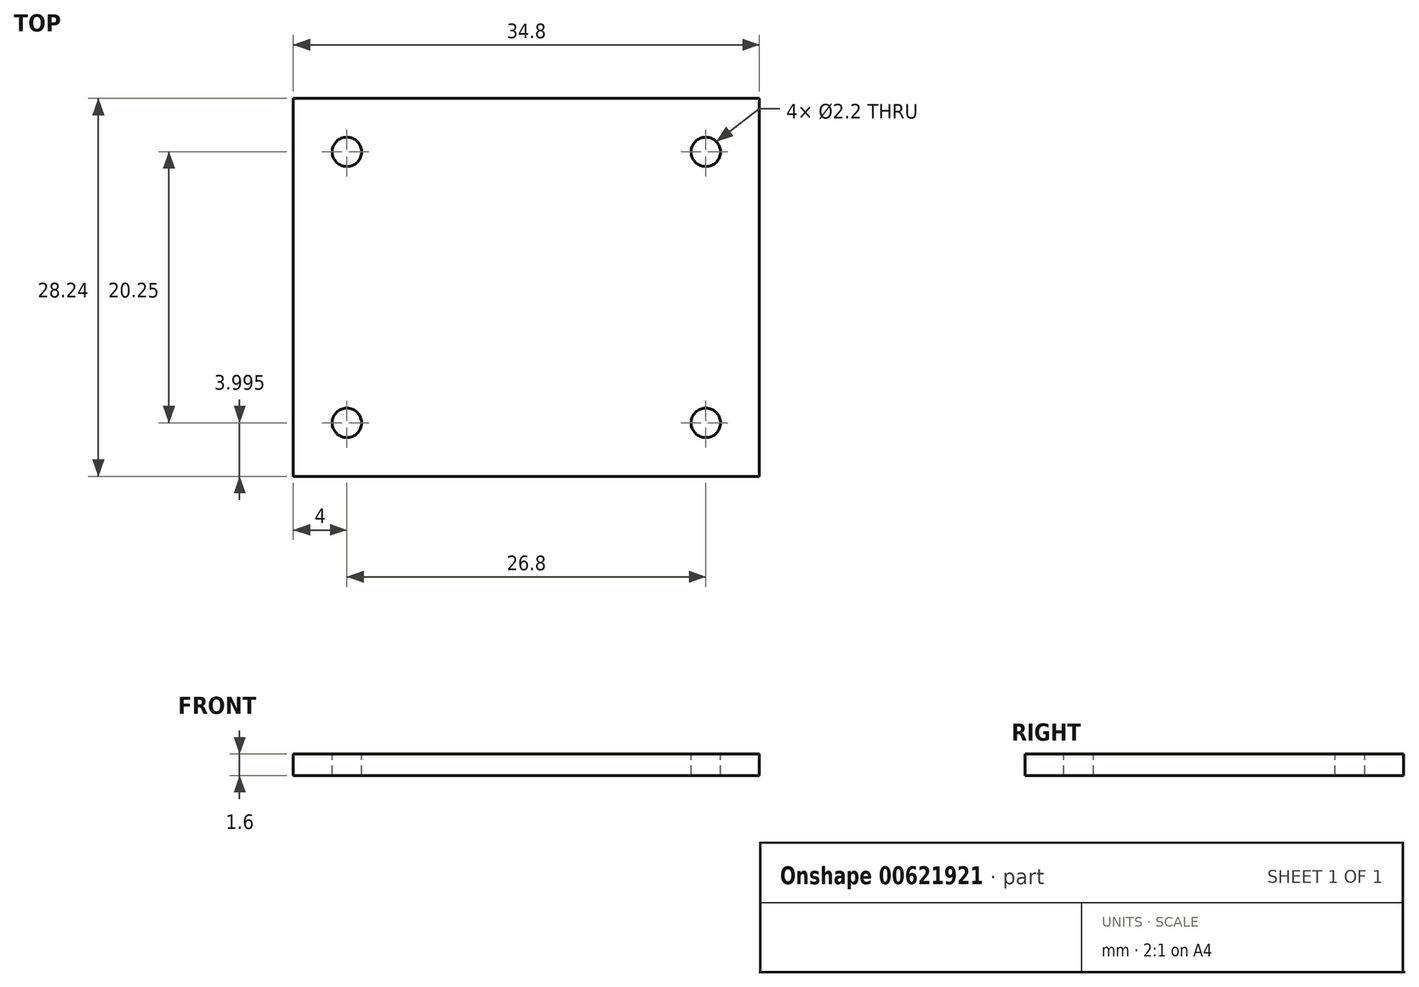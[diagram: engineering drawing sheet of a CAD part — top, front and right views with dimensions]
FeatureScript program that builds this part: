
annotation { "Feature Type Name" : "Feature", "Feature Type Description" : "" }
export const myFeature = defineFeature(function(context is Context, id is Id, definition is map)
    precondition{}
    {
        {
            var Q0;
            Q0=qCreatedBy(makeId("Top.planeOp"),FACE);
            var sketch = newSketch(context, id + "F0", { "sketchPlane" : qUnion([Q0])});
            skLineSegment(sketch, "E0.bottom", {"start": v(-17.4, 14.12) * mm, "end": v(17.4, 14.12) * mm});
            skLineSegment(sketch, "E0.top", {"start": v(-17.4, -14.13) * mm, "end": v(17.4, -14.13) * mm});
            skLineSegment(sketch, "E0.left", {"start": v(-17.4, 14.12) * mm, "end": v(-17.4, -14.13) * mm});
            skLineSegment(sketch, "E0.right", {"start": v(17.4, 14.12) * mm, "end": v(17.4, -14.12) * mm});
            skLineSegment(sketch, "E1", {"start": v(-17.4, 14.13) * mm, "end": v(17.4, -14.13) * mm});
            skSolve(sketch);
        }
        {
            var Q0;
            Q0=makeQuery(id+"F0.imprint","IMPRINT",FACE,{"disambiguationData":[TD([[makeQuery(id+"F0.imprint","IMPRINT",EDGE,{"derivedFrom":sQuery(id+"F0.wireOp",EDGE,"E0.top")}),1.0]])]});
            var Q1;
            Q1=makeQuery(id+"F0.imprint","IMPRINT",FACE,{"disambiguationData":[TD([[makeQuery(id+"F0.imprint","IMPRINT",EDGE,{"derivedFrom":sQuery(id+"F0.wireOp",EDGE,"E0.bottom")}),-1.0]])]});
            extrude(context, id + "F1", {"entities" : qUnion([Q0, Q1]), "depth" : 1.6 * mm, "offsetDistance" : 25 * mm});
        }
        {
            var Q0;
            Q0=makeQuery(id+"F1.opExtrude","CAP_FACE",FACE,{"disambiguationData":[OSD([sQuery(id+"F0.wireOp",EDGE,"E0.bottom"),sQuery(id+"F0.wireOp",EDGE,"E0.top"),sQuery(id+"F0.wireOp",EDGE,"E0.left"),sQuery(id+"F0.wireOp",EDGE,"E0.right")])],"isStart":false});
            var sketch = newSketch(context, id + "F2", { "sketchPlane" : qUnion([Q0])});
            skCircle(sketch, "E2", {"center": v(-13.4, -10.13) * mm, "radius": 1.1 * mm});
            skCircle(sketch, "E3", {"center": v(-13.4, 10.12) * mm, "radius": 1.1 * mm});
            skCircle(sketch, "E4", {"center": v(13.4, 10.12) * mm, "radius": 1.1 * mm});
            skCircle(sketch, "E5", {"center": v(13.4, -10.13) * mm, "radius": 1.1 * mm});
            skLineSegment(sketch, "E6", {"start": v(-13.4, 10.12) * mm, "end": v(-13.4, -10.13) * mm});
            skLineSegment(sketch, "E7", {"start": v(-13.4, -10.13) * mm, "end": v(13.4, -10.13) * mm});
            skLineSegment(sketch, "E8", {"start": v(13.4, -10.13) * mm, "end": v(13.4, 10.12) * mm});
            skLineSegment(sketch, "E9", {"start": v(-13.4, 10.12) * mm, "end": v(13.4, 10.12) * mm});
            skSolve(sketch);
        }
        {
            var Q0;
            {var subQ0=sQuery(id+"F2.wireOp",EDGE,"E6");var subQ1=sQuery(id+"F2.wireOp",EDGE,"E3");var subQ2=makeQuery(id+"F2.imprint","INTERSECT",VERTEX,{"derivedFrom":[subQ1,subQ0]});Q0=makeQuery(id+"F2.imprint","IMPRINT",FACE,{"disambiguationData":[TD([[makeQuery(id+"F2.imprint","IMPRINT",EDGE,{"disambiguationData":[TD([[subQ2,-1.0]])],"derivedFrom":subQ1}),1.0]])]});}
            var Q1;
            {var subQ0=sQuery(id+"F2.wireOp",EDGE,"E6");var subQ1=sQuery(id+"F2.wireOp",EDGE,"E3");var subQ2=makeQuery(id+"F2.imprint","INTERSECT",VERTEX,{"derivedFrom":[subQ1,subQ0]});Q1=makeQuery(id+"F2.imprint","IMPRINT",FACE,{"disambiguationData":[TD([[makeQuery(id+"F2.imprint","IMPRINT",EDGE,{"disambiguationData":[TD([[subQ2,1.0]])],"derivedFrom":subQ1}),1.0]])]});}
            var Q2;
            {var subQ0=sQuery(id+"F2.wireOp",EDGE,"E6");var subQ1=sQuery(id+"F2.wireOp",EDGE,"E2");var subQ2=makeQuery(id+"F2.imprint","INTERSECT",VERTEX,{"derivedFrom":[subQ1,subQ0]});Q2=makeQuery(id+"F2.imprint","IMPRINT",FACE,{"disambiguationData":[TD([[makeQuery(id+"F2.imprint","IMPRINT",EDGE,{"disambiguationData":[TD([[subQ2,1.0]])],"derivedFrom":subQ1}),1.0]])]});}
            var Q3;
            {var subQ0=sQuery(id+"F2.wireOp",EDGE,"E6");var subQ1=sQuery(id+"F2.wireOp",EDGE,"E2");var subQ2=makeQuery(id+"F2.imprint","INTERSECT",VERTEX,{"derivedFrom":[subQ1,subQ0]});Q3=makeQuery(id+"F2.imprint","IMPRINT",FACE,{"disambiguationData":[TD([[makeQuery(id+"F2.imprint","IMPRINT",EDGE,{"disambiguationData":[TD([[subQ2,-1.0]])],"derivedFrom":subQ1}),1.0]])]});}
            var Q4;
            {var subQ0=sQuery(id+"F2.wireOp",EDGE,"E7");var subQ1=sQuery(id+"F2.wireOp",EDGE,"E5");var subQ2=makeQuery(id+"F2.imprint","INTERSECT",VERTEX,{"derivedFrom":[subQ1,subQ0]});Q4=makeQuery(id+"F2.imprint","IMPRINT",FACE,{"disambiguationData":[TD([[makeQuery(id+"F2.imprint","IMPRINT",EDGE,{"disambiguationData":[TD([[subQ2,1.0]])],"derivedFrom":subQ1}),1.0]])]});}
            var Q5;
            {var subQ0=sQuery(id+"F2.wireOp",EDGE,"E7");var subQ1=sQuery(id+"F2.wireOp",EDGE,"E5");var subQ2=makeQuery(id+"F2.imprint","INTERSECT",VERTEX,{"derivedFrom":[subQ1,subQ0]});Q5=makeQuery(id+"F2.imprint","IMPRINT",FACE,{"disambiguationData":[TD([[makeQuery(id+"F2.imprint","IMPRINT",EDGE,{"disambiguationData":[TD([[subQ2,-1.0]])],"derivedFrom":subQ1}),1.0]])]});}
            var Q6;
            {var subQ0=sQuery(id+"F2.wireOp",EDGE,"E8");var subQ1=sQuery(id+"F2.wireOp",EDGE,"E4");var subQ2=makeQuery(id+"F2.imprint","INTERSECT",VERTEX,{"derivedFrom":[subQ1,subQ0]});Q6=makeQuery(id+"F2.imprint","IMPRINT",FACE,{"disambiguationData":[TD([[makeQuery(id+"F2.imprint","IMPRINT",EDGE,{"disambiguationData":[TD([[subQ2,1.0]])],"derivedFrom":subQ1}),1.0]])]});}
            var Q7;
            {var subQ0=sQuery(id+"F2.wireOp",EDGE,"E8");var subQ1=sQuery(id+"F2.wireOp",EDGE,"E4");var subQ2=makeQuery(id+"F2.imprint","INTERSECT",VERTEX,{"derivedFrom":[subQ1,subQ0]});Q7=makeQuery(id+"F2.imprint","IMPRINT",FACE,{"disambiguationData":[TD([[makeQuery(id+"F2.imprint","IMPRINT",EDGE,{"disambiguationData":[TD([[subQ2,-1.0]])],"derivedFrom":subQ1}),1.0]])]});}
            extrude(context, id + "F3", {"entities" : qUnion([Q0, Q1, Q2, Q3, Q4, Q5, Q6, Q7]), "operationType" : NewBodyOperationType.REMOVE, "endBound" : BoundingType.THROUGH_ALL, "oppositeDirection" : true, "depth" : 25 * mm, "offsetDistance" : 25 * mm});
        }
    });
